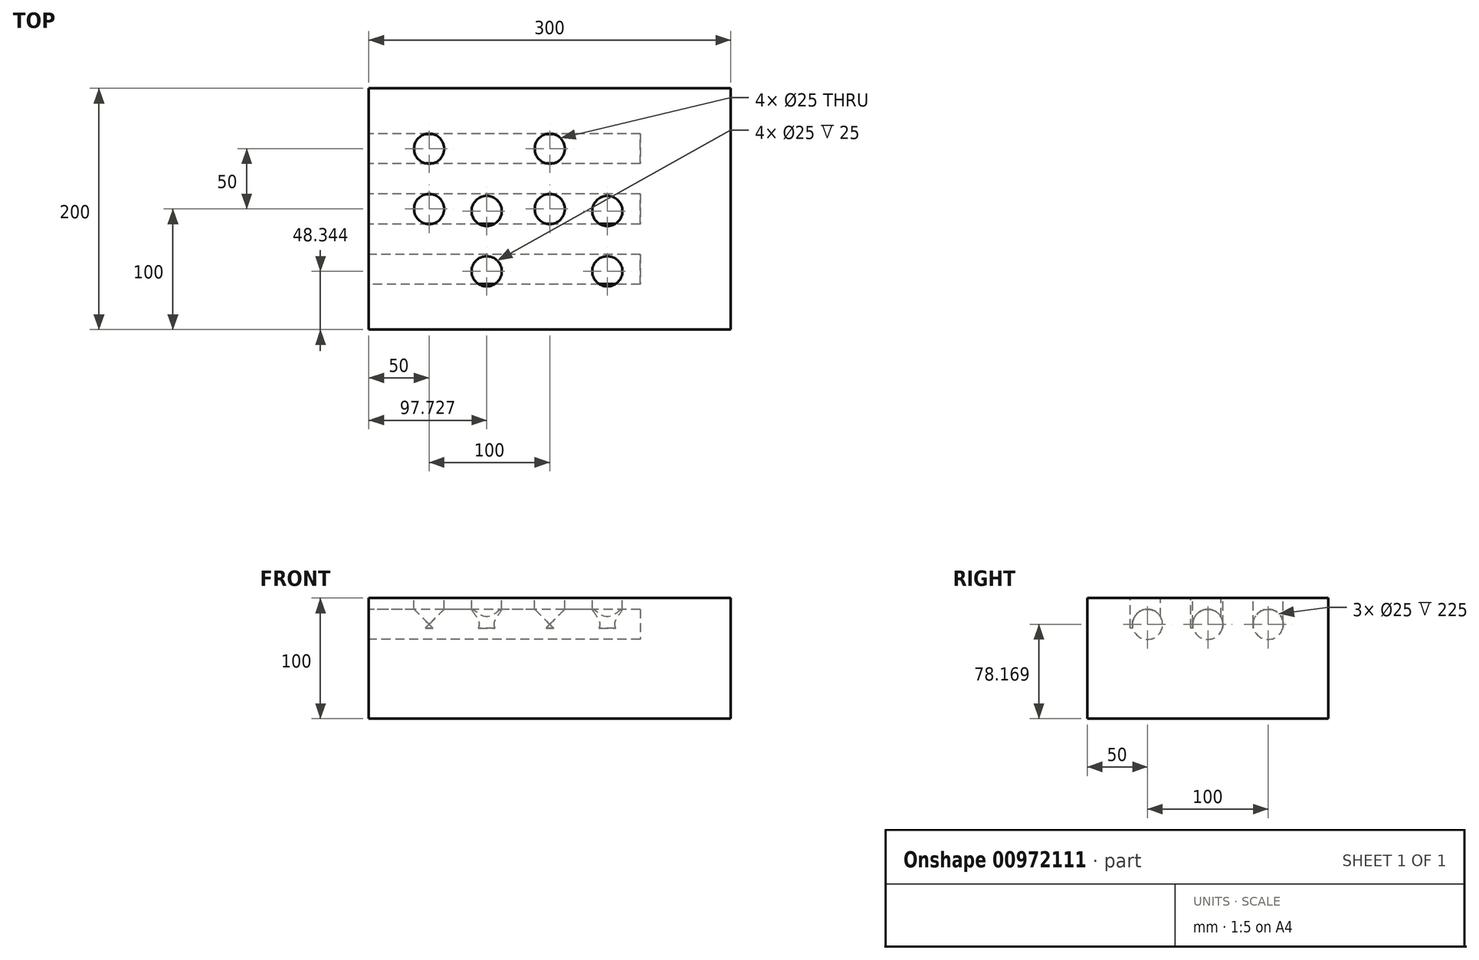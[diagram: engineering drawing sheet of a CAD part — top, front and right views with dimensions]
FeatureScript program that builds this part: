
annotation { "Feature Type Name" : "Feature", "Feature Type Description" : "" }
export const myFeature = defineFeature(function(context is Context, id is Id, definition is map)
    precondition{}
    {
        {
            var Q0;
            Q0=qCreatedBy(makeId("Right.planeOp"),FACE);
            var sketch = newSketch(context, id + "F0", { "sketchPlane" : qUnion([Q0])});
            skLineSegment(sketch, "E0.bottom", {"start": v(100, 0) * mm, "end": v(-100, 0) * mm});
            skLineSegment(sketch, "E0.top", {"start": v(100, 100) * mm, "end": v(-100, 100) * mm});
            skLineSegment(sketch, "E0.left", {"start": v(100, 0) * mm, "end": v(100, 100) * mm});
            skLineSegment(sketch, "E0.right", {"start": v(-100, 0) * mm, "end": v(-100, 100) * mm});
            skSolve(sketch);
        }
        {
            var Q0;
            Q0=makeQuery(id+"F0.imprint","IMPRINT",FACE,{"disambiguationData":[TD([[makeQuery(id+"F0.imprint","IMPRINT",EDGE,{"derivedFrom":sQuery(id+"F0.wireOp",EDGE,"E0.bottom")}),-1.0]])]});
            extrude(context, id + "F1", {"entities" : qUnion([Q0]), "depth" : 300 * mm, "offsetDistance" : 25 * mm});
        }
        {
            var Q0;
            Q0=makeQuery(id+"F1.opExtrude","CAP_FACE",FACE,{"disambiguationData":[OSD([sQuery(id+"F0.wireOp",EDGE,"E0.bottom"),sQuery(id+"F0.wireOp",EDGE,"E0.top"),sQuery(id+"F0.wireOp",EDGE,"E0.left"),sQuery(id+"F0.wireOp",EDGE,"E0.right")])],"isStart":true});
            var sketch = newSketch(context, id + "F2", { "sketchPlane" : qUnion([Q0])});
            skCircle(sketch, "E1", {"center": v(-50, 78.17) * mm, "radius": 12.5 * mm});
            skCircle(sketch, "E2", {"center": v(0, 78.17) * mm, "radius": 12.5 * mm});
            skCircle(sketch, "E3", {"center": v(50, 78.17) * mm, "radius": 12.5 * mm});
            skSolve(sketch);
        }
        {
            var Q0;
            Q0=makeQuery(id+"F2.imprint","IMPRINT",FACE,{"disambiguationData":[TD([[makeQuery(id+"F2.imprint","IMPRINT",EDGE,{"derivedFrom":sQuery(id+"F2.wireOp",EDGE,"E1")}),1.0]])]});
            var Q1;
            Q1=makeQuery(id+"F2.imprint","IMPRINT",FACE,{"disambiguationData":[TD([[makeQuery(id+"F2.imprint","IMPRINT",EDGE,{"derivedFrom":sQuery(id+"F2.wireOp",EDGE,"E2")}),1.0]])]});
            var Q2;
            Q2=makeQuery(id+"F2.imprint","IMPRINT",FACE,{"disambiguationData":[TD([[makeQuery(id+"F2.imprint","IMPRINT",EDGE,{"derivedFrom":sQuery(id+"F2.wireOp",EDGE,"E3")}),1.0]])]});
            extrude(context, id + "F3", {"entities" : qUnion([Q0, Q1, Q2]), "operationType" : NewBodyOperationType.REMOVE, "oppositeDirection" : true, "depth" : 225 * mm, "offsetDistance" : 25 * mm});
        }
        {
            var Q0;
            Q0=makeQuery(id+"F1.opExtrude","SWEPT_FACE",FACE,{"disambiguationData":[OSD([sQuery(id+"F0.wireOp",EDGE,"E0.top")])]});
            var sketch = newSketch(context, id + "F4", { "sketchPlane" : qUnion([Q0])});
            skCircle(sketch, "E4", {"center": v(50, 50) * mm, "radius": 12.5 * mm});
            skCircle(sketch, "E5", {"center": v(50, 0) * mm, "radius": 12.5 * mm});
            skCircle(sketch, "E6", {"center": v(150, 50) * mm, "radius": 12.5 * mm});
            skCircle(sketch, "E7", {"center": v(150, 0) * mm, "radius": 12.5 * mm});
            skCircle(sketch, "E8", {"center": v(97.73, -1.66) * mm, "radius": 12.5 * mm});
            skCircle(sketch, "E9", {"center": v(97.73, -51.66) * mm, "radius": 12.5 * mm});
            skCircle(sketch, "E10", {"center": v(197.73, -1.66) * mm, "radius": 12.5 * mm});
            skCircle(sketch, "E11", {"center": v(197.73, -51.66) * mm, "radius": 12.5 * mm});
            skSolve(sketch);
        }
        {
            var Q0;
            Q0 = qSketchRegion(id + "F4", true);
            extrude(context, id + "F5", {"entities" : qUnion([Q0]), "operationType" : NewBodyOperationType.REMOVE, "oppositeDirection" : true, "depth" : 25 * mm, "offsetDistance" : 25 * mm});
        }
    });
